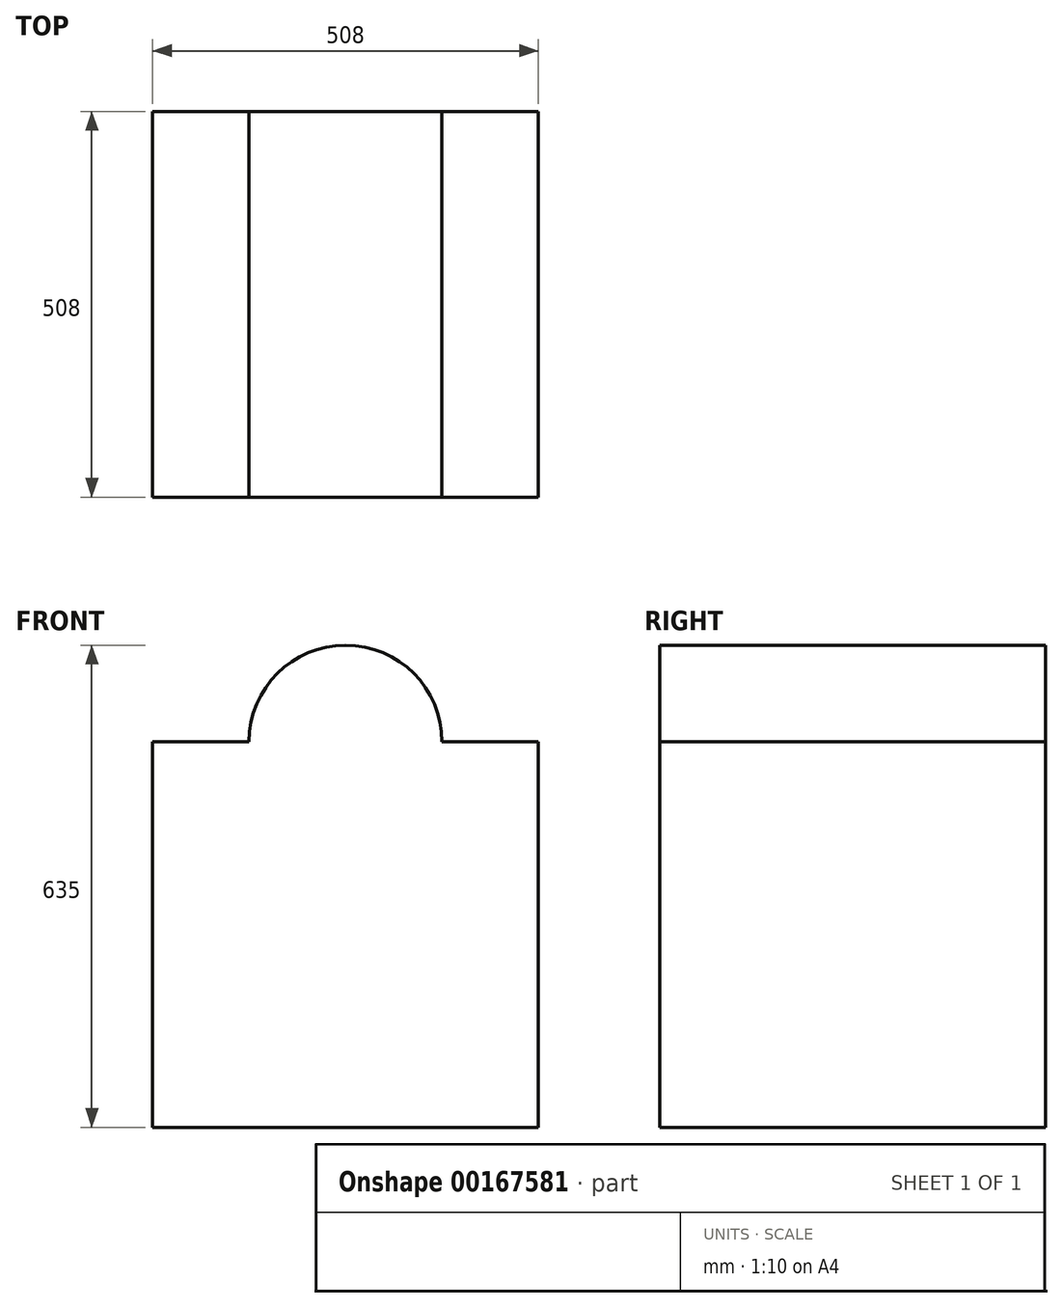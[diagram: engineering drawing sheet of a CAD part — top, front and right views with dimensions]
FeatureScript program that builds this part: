
annotation { "Feature Type Name" : "Feature", "Feature Type Description" : "" }
export const myFeature = defineFeature(function(context is Context, id is Id, definition is map)
    precondition{}
    {
        {
            var Q0;
            Q0=qCreatedBy(makeId("Front.planeOp"),FACE);
            var sketch = newSketch(context, id + "F0", { "sketchPlane" : qUnion([Q0])});
            skLineSegment(sketch, "E0.bottom", {"start": v(-254, 254) * mm, "end": v(-127, 254) * mm});
            skLineSegment(sketch, "E0.top", {"start": v(-254, -254) * mm, "end": v(254, -254) * mm});
            skLineSegment(sketch, "E0.left", {"start": v(-254, 254) * mm, "end": v(-254, -254) * mm});
            skLineSegment(sketch, "E0.right", {"start": v(254, 254) * mm, "end": v(254, -254) * mm});
            skArc(sketch, "E1", {"start": v(127, 254) * mm, "mid": v(0, 381) * mm, "end": v(-127, 254) * mm});
            skLineSegment(sketch, "E2.trimOffspring", {"start": v(127, 254) * mm, "end": v(254, 254) * mm});
            skSolve(sketch);
        }
        {
            var Q0;
            Q0=makeQuery(id+"F0.imprint","IMPRINT",FACE,{"disambiguationData":[TD([[makeQuery(id+"F0.imprint","IMPRINT",EDGE,{"derivedFrom":sQuery(id+"F0.wireOp",EDGE,"E0.bottom")}),-1.0]])]});
            extrude(context, id + "F1", {"entities" : qUnion([Q0]), "depth" : 508 * mm});
        }
    });
